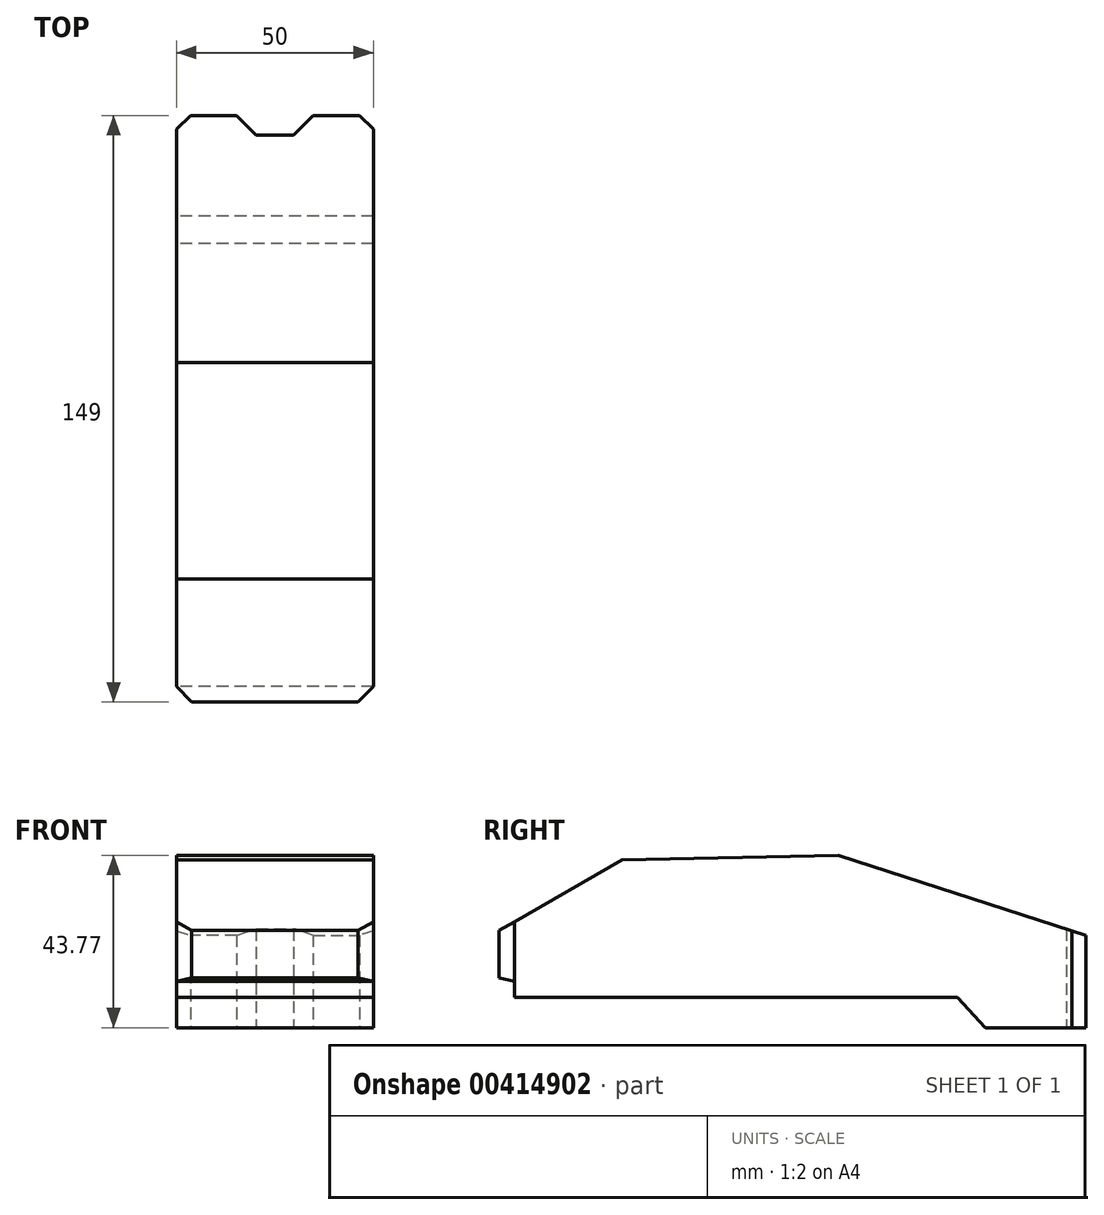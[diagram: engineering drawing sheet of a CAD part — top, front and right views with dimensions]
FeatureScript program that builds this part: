
annotation { "Feature Type Name" : "Feature", "Feature Type Description" : "" }
export const myFeature = defineFeature(function(context is Context, id is Id, definition is map)
    precondition{}
    {
        {
            var Q0;
            Q0=qCreatedBy(makeId("Top.planeOp"),FACE);
            var sketch = newSketch(context, id + "F0", { "sketchPlane" : qUnion([Q0])});
            skLineSegment(sketch, "E0.bottom", {"start": v(0, 0) * mm, "end": v(-25, 0) * mm, "construction": true});
            skLineSegment(sketch, "E0.top", {"start": v(0, 149) * mm, "end": v(-25, 149) * mm, "construction": true});
            skLineSegment(sketch, "E0.left", {"start": v(0, 0) * mm, "end": v(0, 149) * mm, "construction": true});
            skLineSegment(sketch, "E0.right", {"start": v(-25, 0) * mm, "end": v(-25, 149) * mm, "construction": true});
            skLineSegment(sketch, "E1", {"start": v(0, 0) * mm, "end": v(-21.11, 0) * mm});
            skLineSegment(sketch, "E2", {"start": v(-21.11, 0) * mm, "end": v(-25, 3.89) * mm});
            skLineSegment(sketch, "E3", {"start": v(-25, 3.89) * mm, "end": v(-25, 145.46) * mm});
            skLineSegment(sketch, "E4", {"start": v(-25, 145.46) * mm, "end": v(-21.46, 149) * mm});
            skLineSegment(sketch, "E5", {"start": v(-21.46, 149) * mm, "end": v(-9.7, 149) * mm});
            skLineSegment(sketch, "E6", {"start": v(-9.7, 149) * mm, "end": v(-4.75, 144.05) * mm});
            skLineSegment(sketch, "E7", {"start": v(-4.75, 144.05) * mm, "end": v(0, 144.05) * mm});
            skLineSegment(sketch, "E8", {"start": v(0, 144.05) * mm, "end": v(0, 0) * mm});
            skSolve(sketch);
        }
        {
            var Q0;
            Q0 = qSketchRegion(id + "F0", true);
            extrude(context, id + "F1", {"entities" : qUnion([Q0]), "depth" : 48 * mm});
        }
        {
            var Q0;
            Q0=makeQuery(id+"F1.opExtrude","SWEPT_FACE",FACE,{"disambiguationData":[OSD([sQuery(id+"F0.wireOp",EDGE,"E3")])]});
            var sketch = newSketch(context, id + "F2", { "sketchPlane" : qUnion([Q0])});
            skLineSegment(sketch, "E9", {"start": v(-145.46, 0) * mm, "end": v(-123.46, 0) * mm});
            skLineSegment(sketch, "E10", {"start": v(-123.46, 0) * mm, "end": v(-116.39, 7.76) * mm});
            skLineSegment(sketch, "E11", {"start": v(0, 24.7) * mm, "end": v(-31.2, 42.65) * mm});
            skLineSegment(sketch, "E12", {"start": v(-31.2, 42.65) * mm, "end": v(-86.2, 43.77) * mm});
            skLineSegment(sketch, "E13", {"start": v(-86.2, 43.77) * mm, "end": v(-149, 23.5) * mm});
            skLineSegment(sketch, "E14", {"start": v(-149, 23.5) * mm, "end": v(-149, 0) * mm});
            skLineSegment(sketch, "E15", {"start": v(-149, 0) * mm, "end": v(-145.46, 0) * mm});
            skLineSegment(sketch, "E16", {"start": v(0, 24.7) * mm, "end": v(0, 12.7) * mm});
            skLineSegment(sketch, "E17", {"start": v(0, 12.7) * mm, "end": v(-3.89, 11.76) * mm});
            skLineSegment(sketch, "E18", {"start": v(-3.89, 11.76) * mm, "end": v(-3.89, 7.76) * mm});
            skLineSegment(sketch, "E19", {"start": v(-3.89, 7.76) * mm, "end": v(-116.39, 7.76) * mm});
            skLineSegment(sketch, "E20", {"start": v(-149, 23.5) * mm, "end": v(-149, 48) * mm});
            skLineSegment(sketch, "E21", {"start": v(-149, 48) * mm, "end": v(0, 48) * mm});
            skLineSegment(sketch, "E22", {"start": v(0, 48) * mm, "end": v(0, 24.7) * mm});
            skLineSegment(sketch, "E23", {"start": v(0, 12.7) * mm, "end": v(0, 0) * mm});
            skLineSegment(sketch, "E24", {"start": v(0, 0) * mm, "end": v(-123.46, 0) * mm});
            skSolve(sketch);
        }
        {
            var Q0;
            {var subQ1=sQuery(id+"F2.wireOp",EDGE,"E12");Q0=makeQuery(id+"F2.imprint","IMPRINT",FACE,{"disambiguationData":[TD([[makeQuery(id+"F2.imprint","IMPRINT",EDGE,{"derivedFrom":subQ1}),-1.0]])]});}
            var Q1;
            {var subQ0=sQuery(id+"F2.wireOp",EDGE,"E10");Q1=makeQuery(id+"F2.imprint","IMPRINT",FACE,{"disambiguationData":[TD([[makeQuery(id+"F2.imprint","IMPRINT",EDGE,{"derivedFrom":subQ0}),-1.0]])]});}
            var Q2;
            {var subQ0=sQuery(id+"F2.wireOp",EDGE,"E20");Q2=makeQuery(id+"F2.imprint","IMPRINT",FACE,{"disambiguationData":[TD([[makeQuery(id+"F2.imprint","IMPRINT",EDGE,{"derivedFrom":subQ0}),-1.0]])]});}
            var Q3;
            {var subQ0=sQuery(id+"F2.wireOp",EDGE,"E22");Q3=makeQuery(id+"F2.imprint","IMPRINT",FACE,{"disambiguationData":[TD([[makeQuery(id+"F2.imprint","IMPRINT",EDGE,{"derivedFrom":subQ0}),-1.0]])]});}
            var Q4;
            Q4=makeQuery(id+"F2.imprint","IMPRINT",FACE,{"disambiguationData":[TD([[makeQuery(id+"F2.imprint","IMPRINT",EDGE,{"derivedFrom":sQuery(id+"F2.wireOp",EDGE,"E17")}),1.0]])]});
            var Q5;
            Q5=makeQuery(id+"F1.opExtrude","SWEPT_FACE",FACE,{"disambiguationData":[OSD([sQuery(id+"F0.wireOp",EDGE,"E8")])]});
            extrude(context, id + "F3", {"entities" : qUnion([Q0, Q1, Q2, Q3, Q4]), "operationType" : NewBodyOperationType.REMOVE, "endBound" : BoundingType.UP_TO_SURFACE, "oppositeDirection" : true, "endBoundEntityFace" : qUnion([Q5]), "depth" : 25 * mm});
        }
        {
            var Q0;
            Q0=makeQuery(id+"F1.opExtrude","SWEPT_BODY",BODY,{"disambiguationData":[OSD([sQuery(id+"F0.wireOp",EDGE,"E1"),sQuery(id+"F0.wireOp",EDGE,"E2"),sQuery(id+"F0.wireOp",EDGE,"E3"),sQuery(id+"F0.wireOp",EDGE,"E4"),sQuery(id+"F0.wireOp",EDGE,"E5"),sQuery(id+"F0.wireOp",EDGE,"E6"),sQuery(id+"F0.wireOp",EDGE,"E7"),sQuery(id+"F0.wireOp",EDGE,"E8")])]});
            var Q1;
            Q1=qCreatedBy(makeId("Right.planeOp"),FACE);
            mirror(context, id + "F4", {"operationType" : NewBodyOperationType.ADD, "entities" : qUnion([Q0]), "mirrorPlane" : qUnion([Q1])});
        }
    });
